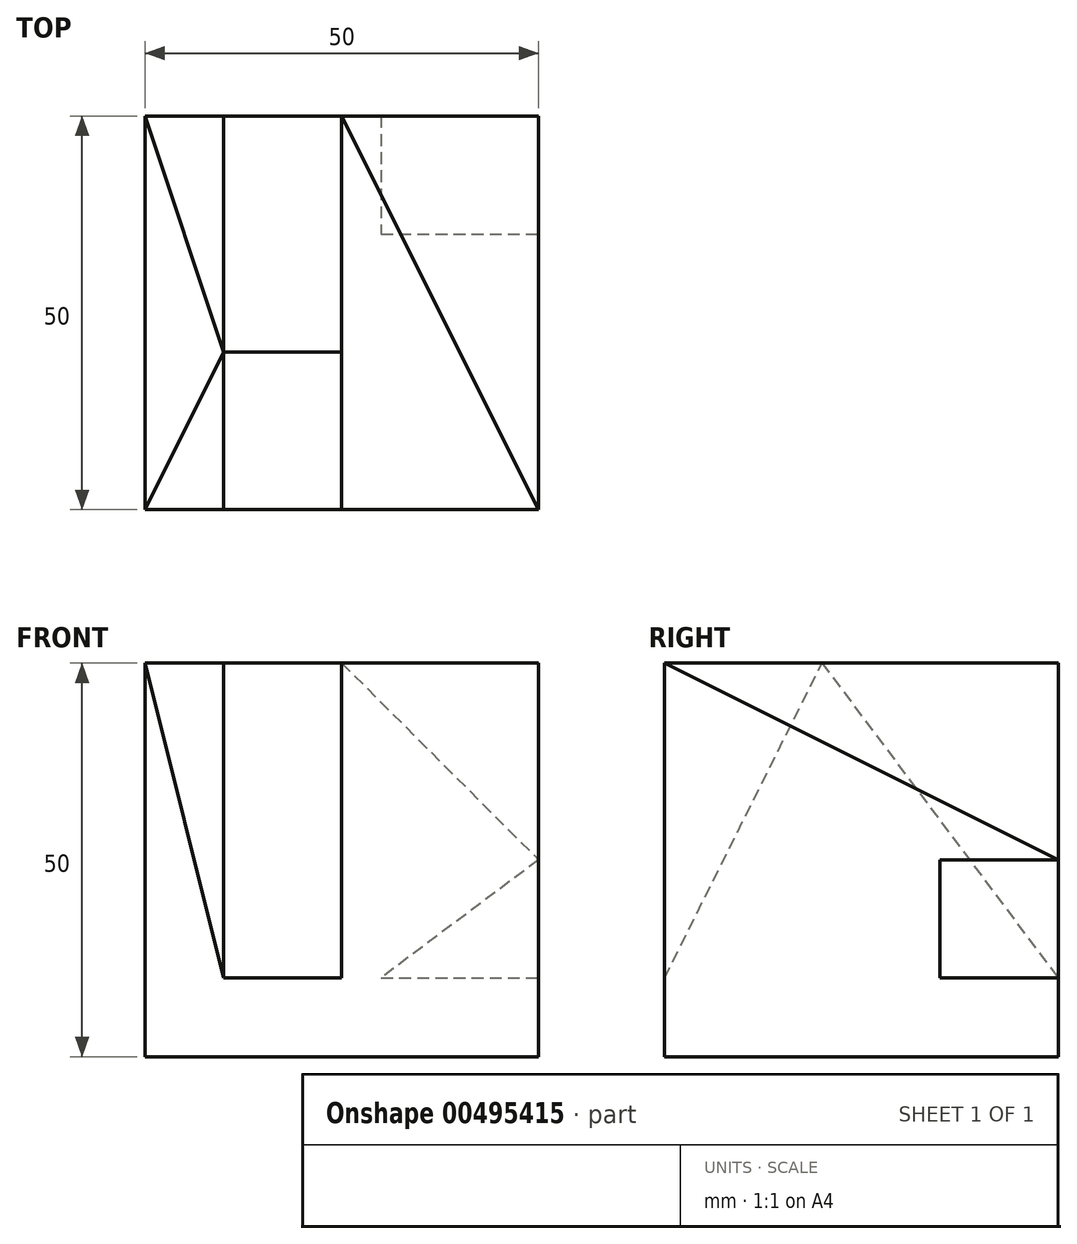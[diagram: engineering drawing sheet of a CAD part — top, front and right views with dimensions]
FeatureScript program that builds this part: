
annotation { "Feature Type Name" : "Feature", "Feature Type Description" : "" }
export const myFeature = defineFeature(function(context is Context, id is Id, definition is map)
    precondition{}
    {
        {
            var Q0;
            Q0=qCreatedBy(makeId("Top.planeOp"),FACE);
            var sketch = newSketch(context, id + "F0", { "sketchPlane" : qUnion([Q0])});
            skLineSegment(sketch, "E0.bottom", {"start": v(0, 0) * mm, "end": v(50, 0) * mm});
            skLineSegment(sketch, "E0.top", {"start": v(0, 50) * mm, "end": v(50, 50) * mm});
            skLineSegment(sketch, "E0.left", {"start": v(0, 0) * mm, "end": v(0, 50) * mm});
            skLineSegment(sketch, "E0.right", {"start": v(50, 0) * mm, "end": v(50, 50) * mm});
            skSolve(sketch);
        }
        {
            var Q0;
            Q0 = qSketchRegion(id + "F0", true);
            extrude(context, id + "F1", {"entities" : qUnion([Q0]), "depth" : 50 * mm});
        }
        {
            var Q0;
            Q0=makeQuery(id+"F1.opExtrude","CAP_FACE",FACE,{"disambiguationData":[OSD([sQuery(id+"F0.wireOp",EDGE,"E0.bottom"),sQuery(id+"F0.wireOp",EDGE,"E0.top"),sQuery(id+"F0.wireOp",EDGE,"E0.left"),sQuery(id+"F0.wireOp",EDGE,"E0.right")])],"isStart":false});
            cPlane(context, id + "F2", {"entities" : qUnion([Q0]), "cplaneType" : CPlaneType.OFFSET, "offset" : 40 * mm, "oppositeDirection" : true, "width" : 150 * mm, "height" : 150 * mm});
        }
        {
            var Q0;
            Q0=makeQuery(id+"F1.opExtrude","SWEPT_FACE",FACE,{"disambiguationData":[OSD([sQuery(id+"F0.wireOp",EDGE,"E0.left")])]});
            cPlane(context, id + "F3", {"entities" : qUnion([Q0]), "cplaneType" : CPlaneType.OFFSET, "offset" : 10 * mm, "oppositeDirection" : true, "width" : 150 * mm, "height" : 150 * mm});
        }
        {
            var Q0;
            Q0=makeQuery(id+"F1.opExtrude","CAP_FACE",FACE,{"disambiguationData":[OSD([sQuery(id+"F0.wireOp",EDGE,"E0.bottom"),sQuery(id+"F0.wireOp",EDGE,"E0.top"),sQuery(id+"F0.wireOp",EDGE,"E0.left"),sQuery(id+"F0.wireOp",EDGE,"E0.right")])],"isStart":false});
            var sketch = newSketch(context, id + "F4", { "sketchPlane" : qUnion([Q0])});
            skPoint(sketch, "E1", {"position": v(10, 20) * mm});
            skSolve(sketch);
        }
        {
            var Q0;
            Q0=makeQuery(id+"F1.opExtrude","SWEPT_FACE",FACE,{"disambiguationData":[OSD([sQuery(id+"F0.wireOp",EDGE,"E0.bottom")])]});
            var sketch = newSketch(context, id + "F5", { "sketchPlane" : qUnion([Q0])});
            skPoint(sketch, "E2", {"position": v(10, 10) * mm});
            skSolve(sketch);
        }
        {
            var Q0;
            Q0=sQuery(id+"F4.wireOp",VERTEX,"E1");
            var Q1;
            Q1=makeQuery(id+"F1.opExtrude","CAP_VERTEX",VERTEX,{"disambiguationData":[OSD([sQuery(id+"F0.wireOp",EDGE,"E0.bottom"),sQuery(id+"F0.wireOp",EDGE,"E0.left")])],"isStart":false});
            var Q2;
            Q2=sQuery(id+"F5.wireOp",VERTEX,"E2");
            cPlane(context, id + "F6", {"entities" : qUnion([Q0, Q1, Q2]), "cplaneType" : CPlaneType.THREE_POINT, "offset" : 25 * mm, "width" : 150 * mm, "height" : 150 * mm});
        }
        {
            var Q0;
            Q0=qCreatedBy(id+"F3.planeOp",FACE);
            var sketch = newSketch(context, id + "F7", { "sketchPlane" : qUnion([Q0])});
            skLineSegment(sketch, "E3", {"start": v(-20, 50) * mm, "end": v(0, 50) * mm});
            skLineSegment(sketch, "E4", {"start": v(0, 50) * mm, "end": v(0, 10) * mm});
            skLineSegment(sketch, "E5", {"start": v(0, 10) * mm, "end": v(-20, 50) * mm});
            skSolve(sketch);
        }
        {
            var Q0;
            Q0 = qSketchRegion(id + "F7", true);
            var Q1;
            Q1=qCreatedBy(id+"F6.planeOp",FACE);
            extrude(context, id + "F8", {"entities" : qUnion([Q0]), "operationType" : NewBodyOperationType.REMOVE, "endBound" : BoundingType.UP_TO_SURFACE, "endBoundEntityFace" : qUnion([Q1]), "depth" : 25 * mm});
        }
        {
            var Q0;
            Q0=makeQuery(id+"F1.opExtrude","SWEPT_FACE",FACE,{"disambiguationData":[OSD([sQuery(id+"F0.wireOp",EDGE,"E0.top")])]});
            var sketch = newSketch(context, id + "F9", { "sketchPlane" : qUnion([Q0])});
            skPoint(sketch, "E6", {"position": v(-10, 10) * mm});
            skSolve(sketch);
        }
        {
            var Q0;
            Q0=makeQuery(id+"F1.opExtrude","CAP_VERTEX",VERTEX,{"disambiguationData":[OSD([sQuery(id+"F0.wireOp",EDGE,"E0.top"),sQuery(id+"F0.wireOp",EDGE,"E0.left")])],"isStart":false});
            var Q1;
            Q1=sQuery(id+"F9.wireOp",VERTEX,"E6");
            var Q2;
            Q2=sQuery(id+"F4.wireOp",VERTEX,"E1");
            cPlane(context, id + "F10", {"entities" : qUnion([Q0, Q1, Q2]), "cplaneType" : CPlaneType.THREE_POINT, "offset" : 25 * mm, "width" : 150 * mm, "height" : 150 * mm});
        }
        {
            var Q0;
            Q0=qCreatedBy(id+"F3.planeOp",FACE);
            var sketch = newSketch(context, id + "F11", { "sketchPlane" : qUnion([Q0])});
            skLineSegment(sketch, "E7", {"start": v(-50, 50) * mm, "end": v(-20, 50) * mm});
            skLineSegment(sketch, "E8", {"start": v(-20, 50) * mm, "end": v(-50, 10) * mm});
            skLineSegment(sketch, "E9", {"start": v(-50, 10) * mm, "end": v(-50, 50) * mm});
            skSolve(sketch);
        }
        {
            var Q0;
            Q0 = qSketchRegion(id + "F11", true);
            var Q1;
            Q1=qCreatedBy(id+"F10.planeOp",FACE);
            extrude(context, id + "F12", {"entities" : qUnion([Q0]), "operationType" : NewBodyOperationType.REMOVE, "endBound" : BoundingType.UP_TO_SURFACE, "endBoundEntityFace" : qUnion([Q1]), "depth" : 25 * mm});
        }
        {
            var Q0;
            Q0=makeQuery(id+"F4.imprint","IMPRINT",FACE,{"disambiguationData":[TD([[makeQuery(id+"F4.imprint","IMPRINT",EDGE,{"derivedFrom":makeQuery(id+"F1.opExtrude","CAP_EDGE",EDGE,{"disambiguationData":[OSD([sQuery(id+"F0.wireOp",EDGE,"E0.bottom")])],"isStart":false})}),1.0]])]});
            var sketch = newSketch(context, id + "F13", { "sketchPlane" : qUnion([Q0])});
            skPoint(sketch, "E10", {"position": v(50, 20) * mm});
            skSolve(sketch);
        }
        {
            var Q0;
            Q0=sQuery(id+"F13.wireOp",VERTEX,"E10");
            var Q1;
            Q1=sQuery(id+"F4.wireOp",VERTEX,"E1");
            var Q2;
            Q2=sQuery(id+"F5.wireOp",VERTEX,"E2");
            cPlane(context, id + "F14", {"entities" : qUnion([Q0, Q1, Q2]), "cplaneType" : CPlaneType.THREE_POINT, "offset" : 25 * mm, "width" : 150 * mm, "height" : 150 * mm});
        }
        {
            var Q0;
            {var subQ0=sQuery(id+"F0.wireOp",EDGE,"E0.bottom");Q0=makeQuery(id+"F5.imprint","IMPRINT",FACE,{"disambiguationData":[TD([[makeQuery(id+"F5.imprint","IMPRINT",EDGE,{"derivedFrom":makeQuery(id+"F1.opExtrude","CAP_EDGE",EDGE,{"disambiguationData":[OSD([subQ0])],"isStart":true})}),1.0]])]});}
            var sketch = newSketch(context, id + "F15", { "sketchPlane" : qUnion([Q0])});
            skLineSegment(sketch, "E11.bottom", {"start": v(25, 50) * mm, "end": v(10, 50) * mm});
            skLineSegment(sketch, "E11.top", {"start": v(25, 10) * mm, "end": v(10, 10) * mm});
            skLineSegment(sketch, "E11.left", {"start": v(25, 50) * mm, "end": v(25, 10) * mm});
            skLineSegment(sketch, "E11.right", {"start": v(10, 50) * mm, "end": v(10, 10) * mm});
            skSolve(sketch);
        }
        {
            var Q0;
            Q0 = qSketchRegion(id + "F15", true);
            var Q1;
            Q1=qCreatedBy(id+"F14.planeOp",FACE);
            extrude(context, id + "F16", {"entities" : qUnion([Q0]), "operationType" : NewBodyOperationType.REMOVE, "endBound" : BoundingType.UP_TO_SURFACE, "oppositeDirection" : true, "endBoundEntityFace" : qUnion([Q1]), "depth" : 25 * mm});
        }
        {
            var Q0;
            Q0=sQuery(id+"F4.wireOp",VERTEX,"E1");
            var Q1;
            Q1=sQuery(id+"F13.wireOp",VERTEX,"E10");
            var Q2;
            Q2=sQuery(id+"F9.wireOp",VERTEX,"E6");
            cPlane(context, id + "F17", {"entities" : qUnion([Q0, Q1, Q2]), "cplaneType" : CPlaneType.THREE_POINT, "offset" : 25 * mm, "width" : 150 * mm, "height" : 150 * mm});
        }
        {
            var Q0;
            {var subQ0=sQuery(id+"F0.wireOp",EDGE,"E0.top");Q0=makeQuery(id+"F9.imprint","IMPRINT",FACE,{"disambiguationData":[TD([[makeQuery(id+"F9.imprint","IMPRINT",EDGE,{"derivedFrom":makeQuery(id+"F1.opExtrude","CAP_EDGE",EDGE,{"disambiguationData":[OSD([subQ0])],"isStart":true})}),-1.0]])]});}
            var sketch = newSketch(context, id + "F18", { "sketchPlane" : qUnion([Q0])});
            skLineSegment(sketch, "E12.bottom", {"start": v(-10, 50) * mm, "end": v(-25, 50) * mm});
            skLineSegment(sketch, "E12.top", {"start": v(-10, 10) * mm, "end": v(-25, 10) * mm});
            skLineSegment(sketch, "E12.left", {"start": v(-10, 50) * mm, "end": v(-10, 10) * mm});
            skLineSegment(sketch, "E12.right", {"start": v(-25, 50) * mm, "end": v(-25, 10) * mm});
            skSolve(sketch);
        }
        {
            var Q0;
            Q0 = qSketchRegion(id + "F18", true);
            var Q1;
            Q1=qCreatedBy(id+"F17.planeOp",FACE);
            extrude(context, id + "F19", {"entities" : qUnion([Q0]), "operationType" : NewBodyOperationType.REMOVE, "endBound" : BoundingType.UP_TO_SURFACE, "oppositeDirection" : true, "endBoundEntityFace" : qUnion([Q1]), "depth" : 25 * mm});
        }
        {
            var Q0;
            Q0=makeQuery(id+"F1.opExtrude","SWEPT_FACE",FACE,{"disambiguationData":[OSD([sQuery(id+"F0.wireOp",EDGE,"E0.right")])]});
            var sketch = newSketch(context, id + "F20", { "sketchPlane" : qUnion([Q0])});
            skPoint(sketch, "E13", {"position": v(0, 25) * mm});
            skPoint(sketch, "E14", {"position": v(50, 25) * mm});
            skSolve(sketch);
        }
        {
            var Q0;
            Q0=makeQuery(id+"F1.opExtrude","SWEPT_FACE",FACE,{"disambiguationData":[OSD([sQuery(id+"F0.wireOp",EDGE,"E0.top")])]});
            var sketch = newSketch(context, id + "F21", { "sketchPlane" : qUnion([Q0])});
            skPoint(sketch, "E15", {"position": v(-30, 10) * mm});
            skSolve(sketch);
        }
        {
            var Q0;
            Q0=sQuery(id+"F20.wireOp",VERTEX,"E13");
            var Q1;
            Q1=sQuery(id+"F21.wireOp",VERTEX,"E15");
            var Q2;
            Q2=sQuery(id+"F20.wireOp",VERTEX,"E14");
            cPlane(context, id + "F22", {"entities" : qUnion([Q0, Q1, Q2]), "cplaneType" : CPlaneType.THREE_POINT, "offset" : 25 * mm, "width" : 150 * mm, "height" : 150 * mm});
        }
        {
            var Q0;
            Q0=makeQuery(id+"F1.opExtrude","SWEPT_FACE",FACE,{"disambiguationData":[OSD([sQuery(id+"F0.wireOp",EDGE,"E0.right")])]});
            var sketch = newSketch(context, id + "F23", { "sketchPlane" : qUnion([Q0])});
            skLineSegment(sketch, "E16.bottom", {"start": v(50, 10) * mm, "end": v(35, 10) * mm});
            skLineSegment(sketch, "E16.top", {"start": v(50, 25) * mm, "end": v(35, 25) * mm});
            skLineSegment(sketch, "E16.left", {"start": v(50, 10) * mm, "end": v(50, 25) * mm});
            skLineSegment(sketch, "E16.right", {"start": v(35, 10) * mm, "end": v(35, 25) * mm});
            skSolve(sketch);
        }
        {
            var Q0;
            Q0=makeQuery(id+"F23.imprint","IMPRINT",FACE,{"disambiguationData":[TD([[makeQuery(id+"F23.imprint","IMPRINT",EDGE,{"derivedFrom":sQuery(id+"F23.wireOp",EDGE,"E16.bottom")}),-1.0]])]});
            var Q1;
            Q1=qCreatedBy(id+"F22.planeOp",FACE);
            extrude(context, id + "F24", {"entities" : qUnion([Q0]), "operationType" : NewBodyOperationType.REMOVE, "endBound" : BoundingType.UP_TO_SURFACE, "oppositeDirection" : true, "endBoundEntityFace" : qUnion([Q1]), "depth" : 25 * mm});
        }
        {
            var Q0;
            Q0=makeQuery(id+"F19.boolean.opBoolean","COPY",VERTEX,{"derivedFrom":makeQuery(id+"F19.opExtrude","CAP_VERTEX",VERTEX,{"disambiguationData":[OSD([sQuery(id+"F0.wireOp",EDGE,"E0.top"),sQuery(id+"F18.wireOp",EDGE,"E12.bottom"),sQuery(id+"F18.wireOp",EDGE,"E12.right")])],"isStart":true})});
            var Q1;
            Q1=makeQuery(id+"F1.opExtrude","CAP_VERTEX",VERTEX,{"disambiguationData":[OSD([sQuery(id+"F0.wireOp",EDGE,"E0.bottom"),sQuery(id+"F0.wireOp",EDGE,"E0.right")])],"isStart":false});
            var Q2;
            Q2=makeQuery(id+"F24.boolean.opBoolean","COPY",VERTEX,{"derivedFrom":makeQuery(id+"F24.opExtrude","CAP_VERTEX",VERTEX,{"disambiguationData":[OSD([sQuery(id+"F0.wireOp",EDGE,"E0.top"),sQuery(id+"F0.wireOp",EDGE,"E0.right"),sQuery(id+"F23.wireOp",EDGE,"E16.top"),sQuery(id+"F23.wireOp",EDGE,"E16.left")])],"isStart":false})});
            cPlane(context, id + "F25", {"entities" : qUnion([Q0, Q1, Q2]), "cplaneType" : CPlaneType.THREE_POINT, "offset" : 25 * mm, "width" : 150 * mm, "height" : 150 * mm});
        }
        {
            var Q0;
            Q0=makeQuery(id+"F1.opExtrude","SWEPT_FACE",FACE,{"disambiguationData":[OSD([sQuery(id+"F0.wireOp",EDGE,"E0.top")])]});
            var sketch = newSketch(context, id + "F26", { "sketchPlane" : qUnion([Q0])});
            skLineSegment(sketch, "E17", {"start": v(-50, 50) * mm, "end": v(-25, 50) * mm});
            skLineSegment(sketch, "E18", {"start": v(-25, 50) * mm, "end": v(-50, 25) * mm});
            skLineSegment(sketch, "E19", {"start": v(-50, 25) * mm, "end": v(-50, 50) * mm});
            skSolve(sketch);
        }
        {
            var Q0;
            Q0 = qSketchRegion(id + "F26", true);
            var Q1;
            Q1=qCreatedBy(id+"F25.planeOp",FACE);
            extrude(context, id + "F27", {"entities" : qUnion([Q0]), "operationType" : NewBodyOperationType.REMOVE, "endBound" : BoundingType.UP_TO_SURFACE, "oppositeDirection" : true, "endBoundEntityFace" : qUnion([Q1]), "depth" : 25 * mm});
        }
    });
